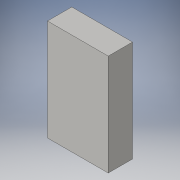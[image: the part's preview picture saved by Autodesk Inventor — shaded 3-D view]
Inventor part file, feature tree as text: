
AUTODESK INVENTOR PART (.ipt)
format: ipt  version: 2016 (Build 200138000, 138)  size: 84,480 bytes
history: native  units: in
note: dims shown in document units (in); Inventor stores cm internally (conversion verified against a paired STEP export)
features: extrude x1, sketch x1
ambient origin geometry x8: Origin, YZ Plane, XZ Plane, XY Plane, X Axis, Y Axis, Z Axis, Center Point
bodies: Solid1 (feature_tree)
feature tree (2):
  extrude  "Extrusion1"  Depth=0.5906in
  sketch  "Sketch1"  dims[d0=0.9843in d1=0.5906in d2=0.2362in d3=0.0in]
